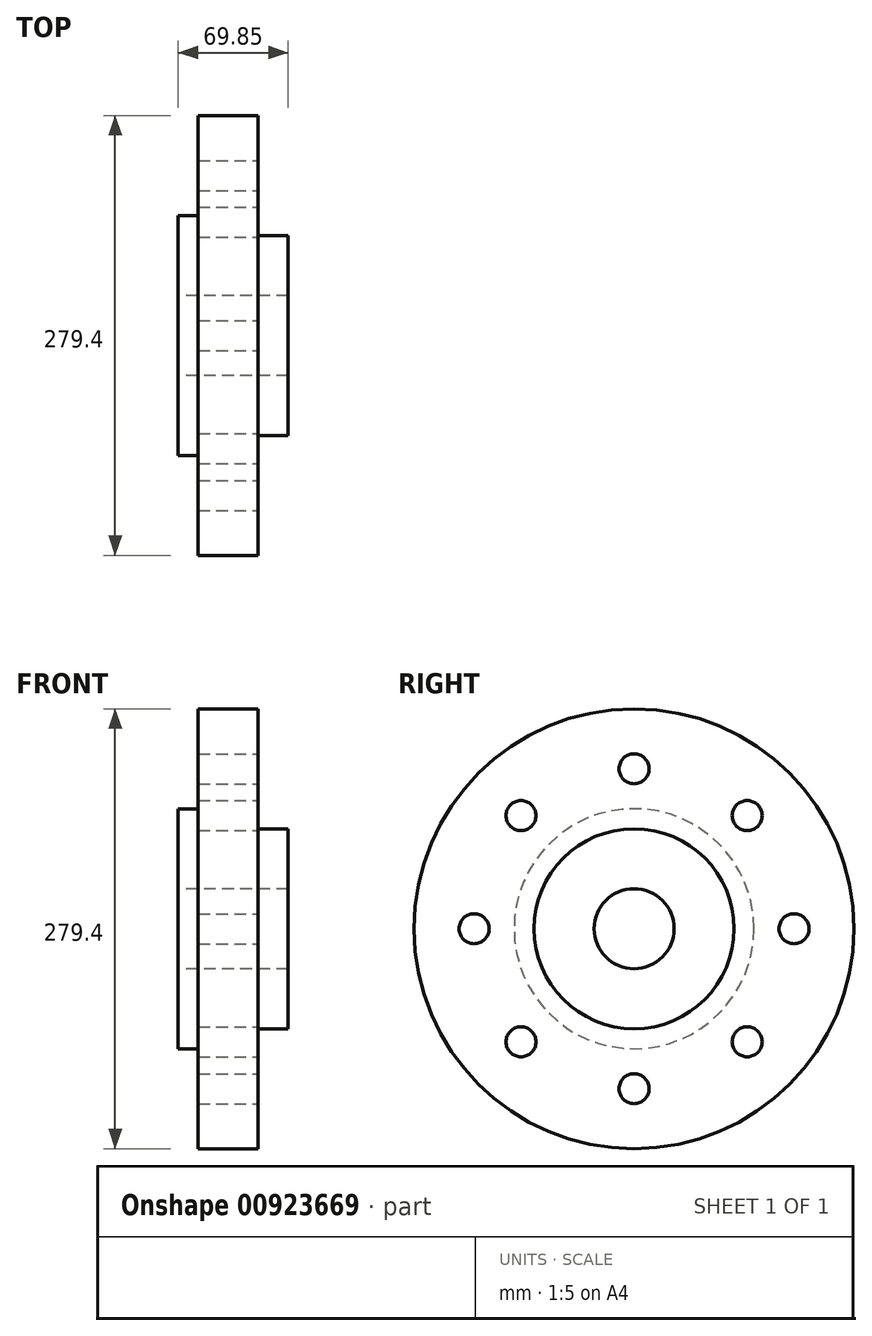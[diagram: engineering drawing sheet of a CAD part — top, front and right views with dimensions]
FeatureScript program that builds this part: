
annotation { "Feature Type Name" : "Feature", "Feature Type Description" : "" }
export const myFeature = defineFeature(function(context is Context, id is Id, definition is map)
    precondition{}
    {
        {
            var Q0;
            Q0=qCreatedBy(makeId("Front.planeOp"),FACE);
            var sketch = newSketch(context, id + "F0", { "sketchPlane" : qUnion([Q0])});
            skLineSegment(sketch, "E0", {"start": v(-239.15, 0) * mm, "end": v(234.4, 0) * mm, "construction": true});
            skLineSegment(sketch, "E1", {"start": v(0, 25.4) * mm, "end": v(0, 76.2) * mm});
            skLineSegment(sketch, "E2", {"start": v(0, 76.2) * mm, "end": v(12.7, 76.2) * mm});
            skLineSegment(sketch, "E3", {"start": v(12.7, 76.2) * mm, "end": v(12.7, 139.7) * mm});
            skLineSegment(sketch, "E4", {"start": v(12.7, 139.7) * mm, "end": v(50.8, 139.7) * mm});
            skLineSegment(sketch, "E5", {"start": v(50.8, 139.7) * mm, "end": v(50.8, 63.5) * mm});
            skLineSegment(sketch, "E6", {"start": v(50.8, 63.5) * mm, "end": v(69.85, 63.5) * mm});
            skLineSegment(sketch, "E7", {"start": v(69.85, 63.5) * mm, "end": v(69.85, 25.4) * mm});
            skLineSegment(sketch, "E8", {"start": v(69.85, 25.4) * mm, "end": v(0, 25.4) * mm});
            skSolve(sketch);
        }
        {
            var Q0;
            Q0 = qSketchRegion(id + "F0", true);
            var Q1;
            Q1=sQuery(id+"F0.wireOp",EDGE,"E0");
            revolve(context, id + "F1", {"surfaceOperationType" : NewSurfaceOperationType.NEW, "entities" : qUnion([Q0]), "axis" : qUnion([Q1]), "revolveType" : RevolveType.FULL});
        }
        {
            var Q0;
            Q0=makeQuery(id+"F1.opRevolve","SWEPT_FACE",FACE,{"disambiguationData":[OSD([sQuery(id+"F0.wireOp",EDGE,"E5")])]});
            var sketch = newSketch(context, id + "F2", { "sketchPlane" : qUnion([Q0])});
            skCircle(sketch, "E9", {"center": v(0, 101.6) * mm, "radius": 9.53 * mm});
            skCircle(sketch, "E10", {"center": v(0, 0) * mm, "radius": 101.6 * mm});
            skCircle(sketch, "E11.1.1", {"center": v(-71.84, 71.84) * mm, "radius": 9.53 * mm});
            skCircle(sketch, "E11.2.1", {"center": v(-101.6, 0) * mm, "radius": 9.53 * mm});
            skCircle(sketch, "E11.3.1", {"center": v(-71.84, -71.84) * mm, "radius": 9.53 * mm});
            skCircle(sketch, "E11.4.1", {"center": v(0, -101.6) * mm, "radius": 9.53 * mm});
            skCircle(sketch, "E11.5.1", {"center": v(71.84, -71.84) * mm, "radius": 9.53 * mm});
            skCircle(sketch, "E11.6.1", {"center": v(101.6, 0) * mm, "radius": 9.53 * mm});
            skCircle(sketch, "E11.7.1", {"center": v(71.84, 71.84) * mm, "radius": 9.53 * mm});
            skSolve(sketch);
        }
        {
            var Q0;
            {var subQ0=sQuery(id+"F2.wireOp",EDGE,"E10");var subQ1=sQuery(id+"F2.wireOp",EDGE,"E9");var subQ2=makeQuery(id+"F2.imprint","INTERSECT",VERTEX,{"disambiguationData":[OD(0.0)],"derivedFrom":[subQ1,subQ0]});Q0=makeQuery(id+"F2.imprint","IMPRINT",FACE,{"disambiguationData":[TD([[makeQuery(id+"F2.imprint","IMPRINT",EDGE,{"disambiguationData":[TD([[subQ2,-1.0]])],"derivedFrom":subQ1}),1.0]])]});}
            var Q1;
            {var subQ0=sQuery(id+"F2.wireOp",EDGE,"E10");var subQ1=sQuery(id+"F2.wireOp",EDGE,"E9");var subQ2=makeQuery(id+"F2.imprint","INTERSECT",VERTEX,{"disambiguationData":[OD(0.0)],"derivedFrom":[subQ1,subQ0]});Q1=makeQuery(id+"F2.imprint","IMPRINT",FACE,{"disambiguationData":[TD([[makeQuery(id+"F2.imprint","IMPRINT",EDGE,{"disambiguationData":[TD([[subQ2,1.0]])],"derivedFrom":subQ1}),1.0]])]});}
            var Q2;
            {var subQ0=sQuery(id+"F2.wireOp",EDGE,"E10");var subQ1=sQuery(id+"F2.wireOp",EDGE,"E11.1.1");var subQ2=makeQuery(id+"F2.imprint","INTERSECT",VERTEX,{"disambiguationData":[OD(0.0)],"derivedFrom":[subQ1,subQ0]});Q2=makeQuery(id+"F2.imprint","IMPRINT",FACE,{"disambiguationData":[TD([[makeQuery(id+"F2.imprint","IMPRINT",EDGE,{"disambiguationData":[TD([[subQ2,1.0]])],"derivedFrom":subQ1}),1.0]])]});}
            var Q3;
            {var subQ0=sQuery(id+"F2.wireOp",EDGE,"E10");var subQ1=sQuery(id+"F2.wireOp",EDGE,"E11.1.1");var subQ2=makeQuery(id+"F2.imprint","INTERSECT",VERTEX,{"disambiguationData":[OD(0.0)],"derivedFrom":[subQ1,subQ0]});Q3=makeQuery(id+"F2.imprint","IMPRINT",FACE,{"disambiguationData":[TD([[makeQuery(id+"F2.imprint","IMPRINT",EDGE,{"disambiguationData":[TD([[subQ2,-1.0]])],"derivedFrom":subQ1}),1.0]])]});}
            var Q4;
            {var subQ0=sQuery(id+"F2.wireOp",EDGE,"E10");var subQ1=sQuery(id+"F2.wireOp",EDGE,"E11.2.1");var subQ2=makeQuery(id+"F2.imprint","INTERSECT",VERTEX,{"disambiguationData":[OD(0.0)],"derivedFrom":[subQ1,subQ0]});Q4=makeQuery(id+"F2.imprint","IMPRINT",FACE,{"disambiguationData":[TD([[makeQuery(id+"F2.imprint","IMPRINT",EDGE,{"disambiguationData":[TD([[subQ2,1.0]])],"derivedFrom":subQ1}),1.0]])]});}
            var Q5;
            {var subQ0=sQuery(id+"F2.wireOp",EDGE,"E10");var subQ1=sQuery(id+"F2.wireOp",EDGE,"E11.2.1");var subQ2=makeQuery(id+"F2.imprint","INTERSECT",VERTEX,{"disambiguationData":[OD(0.0)],"derivedFrom":[subQ1,subQ0]});Q5=makeQuery(id+"F2.imprint","IMPRINT",FACE,{"disambiguationData":[TD([[makeQuery(id+"F2.imprint","IMPRINT",EDGE,{"disambiguationData":[TD([[subQ2,-1.0]])],"derivedFrom":subQ1}),1.0]])]});}
            var Q6;
            {var subQ0=sQuery(id+"F2.wireOp",EDGE,"E10");var subQ1=sQuery(id+"F2.wireOp",EDGE,"E11.3.1");var subQ2=makeQuery(id+"F2.imprint","INTERSECT",VERTEX,{"disambiguationData":[OD(0.0)],"derivedFrom":[subQ1,subQ0]});Q6=makeQuery(id+"F2.imprint","IMPRINT",FACE,{"disambiguationData":[TD([[makeQuery(id+"F2.imprint","IMPRINT",EDGE,{"disambiguationData":[TD([[subQ2,-1.0]])],"derivedFrom":subQ1}),1.0]])]});}
            var Q7;
            {var subQ0=sQuery(id+"F2.wireOp",EDGE,"E10");var subQ1=sQuery(id+"F2.wireOp",EDGE,"E11.3.1");var subQ2=makeQuery(id+"F2.imprint","INTERSECT",VERTEX,{"disambiguationData":[OD(0.0)],"derivedFrom":[subQ1,subQ0]});Q7=makeQuery(id+"F2.imprint","IMPRINT",FACE,{"disambiguationData":[TD([[makeQuery(id+"F2.imprint","IMPRINT",EDGE,{"disambiguationData":[TD([[subQ2,1.0]])],"derivedFrom":subQ1}),1.0]])]});}
            var Q8;
            {var subQ0=sQuery(id+"F2.wireOp",EDGE,"E10");var subQ1=sQuery(id+"F2.wireOp",EDGE,"E11.4.1");var subQ2=makeQuery(id+"F2.imprint","INTERSECT",VERTEX,{"disambiguationData":[OD(0.0)],"derivedFrom":[subQ1,subQ0]});Q8=makeQuery(id+"F2.imprint","IMPRINT",FACE,{"disambiguationData":[TD([[makeQuery(id+"F2.imprint","IMPRINT",EDGE,{"disambiguationData":[TD([[subQ2,-1.0]])],"derivedFrom":subQ1}),1.0]])]});}
            var Q9;
            {var subQ0=sQuery(id+"F2.wireOp",EDGE,"E10");var subQ1=sQuery(id+"F2.wireOp",EDGE,"E11.4.1");var subQ2=makeQuery(id+"F2.imprint","INTERSECT",VERTEX,{"disambiguationData":[OD(0.0)],"derivedFrom":[subQ1,subQ0]});Q9=makeQuery(id+"F2.imprint","IMPRINT",FACE,{"disambiguationData":[TD([[makeQuery(id+"F2.imprint","IMPRINT",EDGE,{"disambiguationData":[TD([[subQ2,1.0]])],"derivedFrom":subQ1}),1.0]])]});}
            var Q10;
            {var subQ0=sQuery(id+"F2.wireOp",EDGE,"E10");var subQ1=sQuery(id+"F2.wireOp",EDGE,"E11.5.1");var subQ2=makeQuery(id+"F2.imprint","INTERSECT",VERTEX,{"disambiguationData":[OD(0.0)],"derivedFrom":[subQ1,subQ0]});Q10=makeQuery(id+"F2.imprint","IMPRINT",FACE,{"disambiguationData":[TD([[makeQuery(id+"F2.imprint","IMPRINT",EDGE,{"disambiguationData":[TD([[subQ2,1.0]])],"derivedFrom":subQ1}),1.0]])]});}
            var Q11;
            {var subQ0=sQuery(id+"F2.wireOp",EDGE,"E10");var subQ1=sQuery(id+"F2.wireOp",EDGE,"E11.5.1");var subQ2=makeQuery(id+"F2.imprint","INTERSECT",VERTEX,{"disambiguationData":[OD(0.0)],"derivedFrom":[subQ1,subQ0]});Q11=makeQuery(id+"F2.imprint","IMPRINT",FACE,{"disambiguationData":[TD([[makeQuery(id+"F2.imprint","IMPRINT",EDGE,{"disambiguationData":[TD([[subQ2,-1.0]])],"derivedFrom":subQ1}),1.0]])]});}
            var Q12;
            {var subQ0=sQuery(id+"F2.wireOp",EDGE,"E10");var subQ1=sQuery(id+"F2.wireOp",EDGE,"E11.6.1");var subQ2=makeQuery(id+"F2.imprint","INTERSECT",VERTEX,{"disambiguationData":[OD(0.0)],"derivedFrom":[subQ1,subQ0]});Q12=makeQuery(id+"F2.imprint","IMPRINT",FACE,{"disambiguationData":[TD([[makeQuery(id+"F2.imprint","IMPRINT",EDGE,{"disambiguationData":[TD([[subQ2,-1.0]])],"derivedFrom":subQ1}),1.0]])]});}
            var Q13;
            {var subQ0=sQuery(id+"F2.wireOp",EDGE,"E10");var subQ1=sQuery(id+"F2.wireOp",EDGE,"E11.6.1");var subQ2=makeQuery(id+"F2.imprint","INTERSECT",VERTEX,{"disambiguationData":[OD(0.0)],"derivedFrom":[subQ1,subQ0]});Q13=makeQuery(id+"F2.imprint","IMPRINT",FACE,{"disambiguationData":[TD([[makeQuery(id+"F2.imprint","IMPRINT",EDGE,{"disambiguationData":[TD([[subQ2,1.0]])],"derivedFrom":subQ1}),1.0]])]});}
            var Q14;
            {var subQ0=sQuery(id+"F2.wireOp",EDGE,"E11.7.1");var subQ1=sQuery(id+"F2.wireOp",EDGE,"E10");var subQ2=makeQuery(id+"F2.imprint","INTERSECT",VERTEX,{"disambiguationData":[OD(0.0)],"derivedFrom":[subQ1,subQ0]});Q14=makeQuery(id+"F2.imprint","IMPRINT",FACE,{"disambiguationData":[TD([[makeQuery(id+"F2.imprint","IMPRINT",EDGE,{"disambiguationData":[TD([[subQ2,-1.0]])],"derivedFrom":subQ1}),-1.0]])]});}
            var Q15;
            {var subQ0=sQuery(id+"F2.wireOp",EDGE,"E11.7.1");var subQ1=sQuery(id+"F2.wireOp",EDGE,"E10");var subQ2=makeQuery(id+"F2.imprint","INTERSECT",VERTEX,{"disambiguationData":[OD(0.0)],"derivedFrom":[subQ1,subQ0]});Q15=makeQuery(id+"F2.imprint","IMPRINT",FACE,{"disambiguationData":[TD([[makeQuery(id+"F2.imprint","IMPRINT",EDGE,{"disambiguationData":[TD([[subQ2,-1.0]])],"derivedFrom":subQ1}),1.0]])]});}
            var Q16;
            Q16=sQuery(id+"F2.wireOp",EDGE,"E11.5.1");
            var Q17;
            Q17=sQuery(id+"F2.wireOp",EDGE,"E11.6.1");
            var Q18;
            Q18=sQuery(id+"F2.wireOp",EDGE,"E11.7.1");
            var Q19;
            Q19=sQuery(id+"F2.wireOp",EDGE,"E9");
            var Q20;
            Q20=sQuery(id+"F2.wireOp",EDGE,"E11.1.1");
            var Q21;
            Q21=sQuery(id+"F2.wireOp",EDGE,"E11.2.1");
            var Q22;
            Q22=sQuery(id+"F2.wireOp",EDGE,"E11.3.1");
            var Q23;
            Q23=sQuery(id+"F2.wireOp",EDGE,"E11.4.1");
            extrude(context, id + "F3", {"entities" : qUnion([Q0, Q1, Q2, Q3, Q4, Q5, Q6, Q7, Q8, Q9, Q10, Q11, Q12, Q13, Q14, Q15]), "operationType" : NewBodyOperationType.REMOVE, "surfaceEntities" : qUnion([Q16, Q17, Q18, Q19, Q20, Q21, Q22, Q23]), "endBound" : BoundingType.THROUGH_ALL, "oppositeDirection" : true, "depth" : 25.4 * mm, "offsetDistance" : 25.4 * mm});
        }
    });
